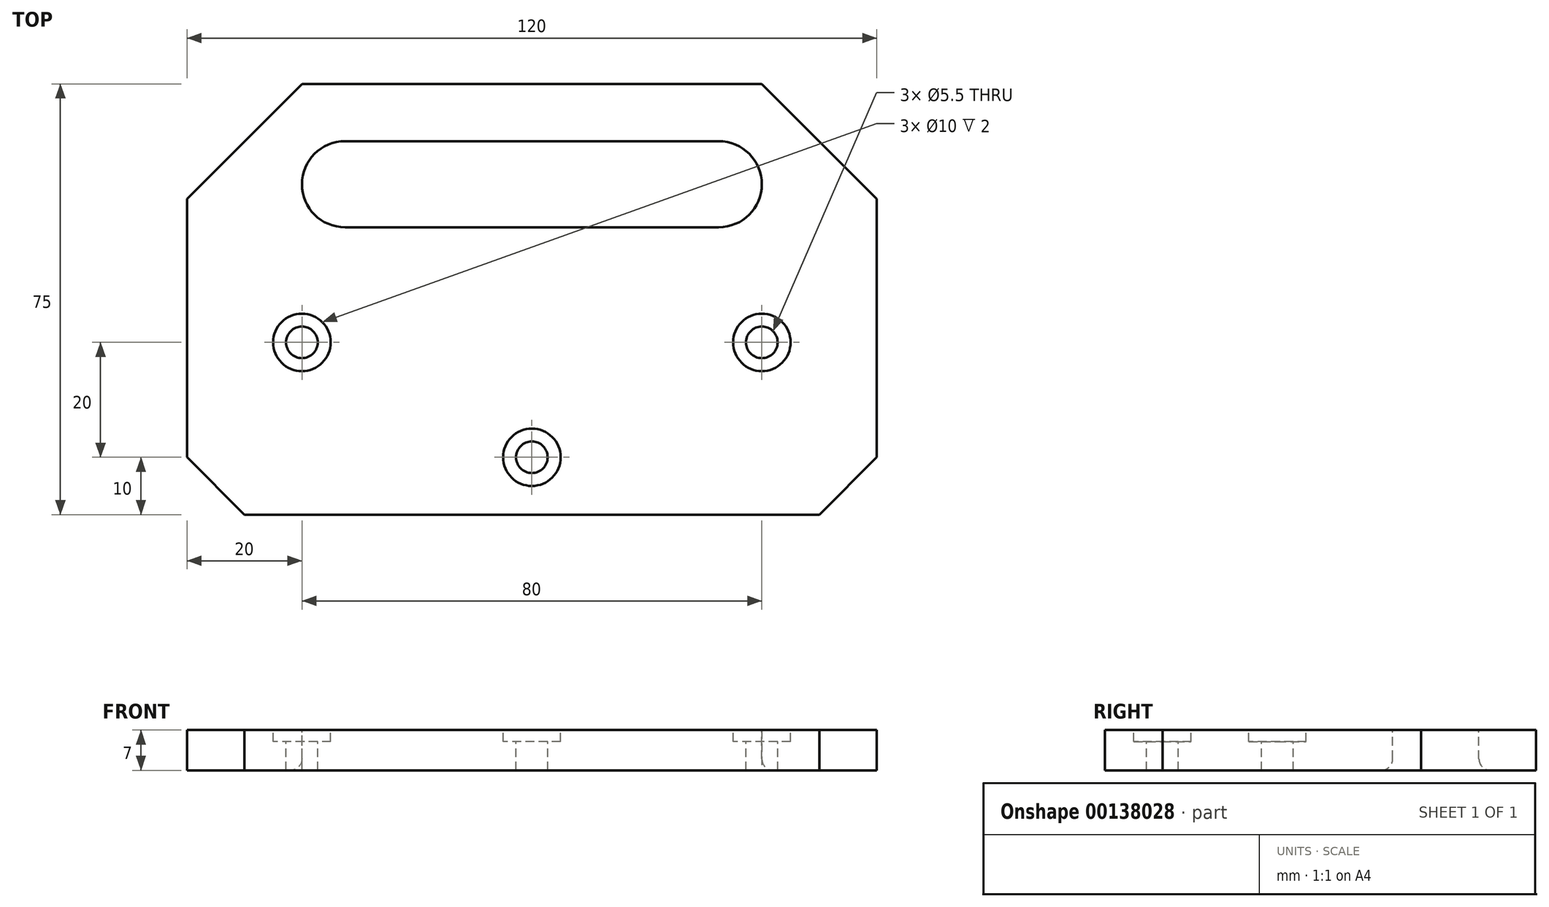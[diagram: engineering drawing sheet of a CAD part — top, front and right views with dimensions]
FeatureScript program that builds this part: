
annotation { "Feature Type Name" : "Feature", "Feature Type Description" : "" }
export const myFeature = defineFeature(function(context is Context, id is Id, definition is map)
    precondition{}
    {
        {
            var Q0;
            Q0=qCreatedBy(makeId("Top.planeOp"),FACE);
            var sketch = newSketch(context, id + "F0", { "sketchPlane" : qUnion([Q0])});
            skLineSegment(sketch, "E0.bottom", {"start": v(60, -37.5) * mm, "end": v(-60, -37.5) * mm});
            skLineSegment(sketch, "E0.top", {"start": v(60, 37.5) * mm, "end": v(-60, 37.5) * mm});
            skLineSegment(sketch, "E0.left", {"start": v(60, -37.5) * mm, "end": v(60, 37.5) * mm});
            skLineSegment(sketch, "E0.right", {"start": v(-60, -37.5) * mm, "end": v(-60, 37.5) * mm});
            skPoint(sketch, "E0.middle", {"position": v(0, 0) * mm});
            skSolve(sketch);
        }
        {
            var Q0;
            Q0=makeQuery(id+"F0.imprint","IMPRINT",FACE,{"disambiguationData":[TD([[makeQuery(id+"F0.imprint","IMPRINT",EDGE,{"derivedFrom":sQuery(id+"F0.wireOp",EDGE,"E0.bottom")}),-1.0]])]});
            extrude(context, id + "F1", {"entities" : qUnion([Q0]), "depth" : 7 * mm});
        }
        {
            var Q0;
            Q0=makeQuery(id+"F1.opExtrude","SWEPT_EDGE",EDGE,{"disambiguationData":[OSD([sQuery(id+"F0.wireOp",EDGE,"E0.top"),sQuery(id+"F0.wireOp",EDGE,"E0.right")])]});
            var Q1;
            Q1=makeQuery(id+"F1.opExtrude","SWEPT_EDGE",EDGE,{"disambiguationData":[OSD([sQuery(id+"F0.wireOp",EDGE,"E0.top"),sQuery(id+"F0.wireOp",EDGE,"E0.left")])]});
            chamfer(context, id + "F2", {"entities" : qUnion([Q0, Q1]), "width" : 20 * mm, "tangentPropagation" : true});
        }
        {
            var Q0;
            Q0=makeQuery(id+"F1.opExtrude","CAP_FACE",FACE,{"disambiguationData":[OSD([sQuery(id+"F0.wireOp",EDGE,"E0.bottom"),sQuery(id+"F0.wireOp",EDGE,"E0.top"),sQuery(id+"F0.wireOp",EDGE,"E0.left"),sQuery(id+"F0.wireOp",EDGE,"E0.right")])],"isStart":false});
            var sketch = newSketch(context, id + "F3", { "sketchPlane" : qUnion([Q0])});
            skLineSegment(sketch, "E1.bottom", {"start": v(32.5, 19.96) * mm, "end": v(-32.5, 19.96) * mm});
            skLineSegment(sketch, "E1.top", {"start": v(32.5, 20.04) * mm, "end": v(-32.5, 20.04) * mm});
            skLineSegment(sketch, "E1.left", {"start": v(32.5, 19.96) * mm, "end": v(32.5, 20.04) * mm});
            skLineSegment(sketch, "E1.right", {"start": v(-32.5, 19.96) * mm, "end": v(-32.5, 20.04) * mm});
            skPoint(sketch, "E1.middle", {"position": v(0, 20) * mm});
            skArc(sketch, "E2.0.startCap", {"start": v(32.5, 27.54) * mm, "mid": v(40, 20.04) * mm, "end": v(32.5, 12.54) * mm});
            skArc(sketch, "E2.0.endCap", {"start": v(-32.5, 12.54) * mm, "mid": v(-40, 20.04) * mm, "end": v(-32.5, 27.54) * mm});
            skLineSegment(sketch, "E2.0.left", {"start": v(32.5, 12.54) * mm, "end": v(-32.5, 12.54) * mm});
            skLineSegment(sketch, "E2.0.right", {"start": v(32.5, 27.54) * mm, "end": v(-32.5, 27.54) * mm});
            skSolve(sketch);
        }
        {
            var Q0;
            Q0=makeQuery(id+"F3.imprint","IMPRINT",FACE,{"disambiguationData":[TD([[makeQuery(id+"F3.imprint","IMPRINT",EDGE,{"derivedFrom":sQuery(id+"F3.wireOp",EDGE,"E1.bottom")}),1.0]])]});
            extrude(context, id + "F4", {"entities" : qUnion([Q0]), "operationType" : NewBodyOperationType.REMOVE, "oppositeDirection" : true, "depth" : 25 * mm});
        }
        {
            var Q0;
            Q0=makeQuery(id+"F4.boolean.opBoolean","COPY",FACE,{"derivedFrom":makeQuery(id+"F4.opExtrude","SWEPT_FACE",FACE,{"disambiguationData":[OSD([sQuery(id+"F3.wireOp",EDGE,"E1.top")])]})});
            extrude(context, id + "F5", {"entities" : qUnion([Q0]), "operationType" : NewBodyOperationType.REMOVE, "oppositeDirection" : true, "depth" : 5 * mm});
        }
        {
            var Q0;
            Q0=makeQuery(id+"F1.opExtrude","SWEPT_EDGE",EDGE,{"disambiguationData":[OSD([sQuery(id+"F0.wireOp",EDGE,"E0.bottom"),sQuery(id+"F0.wireOp",EDGE,"E0.right")])]});
            var Q1;
            Q1=makeQuery(id+"F1.opExtrude","SWEPT_EDGE",EDGE,{"disambiguationData":[OSD([sQuery(id+"F0.wireOp",EDGE,"E0.bottom"),sQuery(id+"F0.wireOp",EDGE,"E0.left")])]});
            chamfer(context, id + "F6", {"entities" : qUnion([Q0, Q1]), "width" : 10 * mm, "tangentPropagation" : true});
        }
        {
            var Q0;
            Q0=makeQuery(id+"F4.boolean.opBoolean","COPY",EDGE,{"derivedFrom":makeQuery(id+"F4.opExtrude","CAP_EDGE",EDGE,{"disambiguationData":[OSD([sQuery(id+"F3.wireOp",EDGE,"E2.0.startCap")])],"isStart":true})});
            var Q1;
            Q1=makeQuery(id+"F4.boolean.opBoolean","INTERSECT",EDGE,{"derivedFrom":[makeQuery(id+"F1.opExtrude","CAP_FACE",FACE,{"disambiguationData":[OSD([sQuery(id+"F0.wireOp",EDGE,"E0.bottom"),sQuery(id+"F0.wireOp",EDGE,"E0.top"),sQuery(id+"F0.wireOp",EDGE,"E0.left"),sQuery(id+"F0.wireOp",EDGE,"E0.right")])],"isStart":true}),makeQuery(id+"F4.opExtrude","SWEPT_FACE",FACE,{"disambiguationData":[OSD([sQuery(id+"F3.wireOp",EDGE,"E2.0.startCap")])]})]});
            fillet(context, id + "F7", {"entities" : qUnion([Q0, Q1]), "radius" : 2 * mm, "tangentPropagation" : true, "allowEdgeOverflow" : false});
        }
        {
            var Q0;
            {var subQ0=sQuery(id+"F0.wireOp",EDGE,"E0.right");var subQ1=sQuery(id+"F0.wireOp",EDGE,"E0.left");var subQ2=sQuery(id+"F0.wireOp",EDGE,"E0.top");var subQ3=sQuery(id+"F0.wireOp",EDGE,"E0.bottom");Q0=makeQuery(id+"F4.boolean.opBoolean","SPLIT",FACE,{"disambiguationData":[TD([makeQuery(id+"F1.opExtrude","SWEPT_FACE",FACE,{"disambiguationData":[OSD([subQ3])]})])],"derivedFrom":makeQuery(id+"F1.opExtrude","CAP_FACE",FACE,{"disambiguationData":[OSD([subQ3,subQ2,subQ1,subQ0])],"isStart":false})});}
            var sketch = newSketch(context, id + "F8", { "sketchPlane" : qUnion([Q0])});
            skPoint(sketch, "E3", {"position": v(0, -27.5) * mm});
            skPoint(sketch, "E4", {"position": v(-40, -7.5) * mm});
            skPoint(sketch, "E5", {"position": v(40, -7.5) * mm});
            skSolve(sketch);
        }
        {
            var Q0;
            Q0=sQuery(id+"F8.wireOp",VERTEX,"E4");
            var Q1;
            Q1=sQuery(id+"F8.wireOp",VERTEX,"E3");
            var Q2;
            Q2=sQuery(id+"F8.wireOp",VERTEX,"E5");
            var Q3;
            Q3=makeQuery(id+"F4.boolean.opBoolean","SPLIT",BODY,{"disambiguationData":[OD(0.0)],"derivedFrom":makeQuery(id+"F1.opExtrude","SWEPT_BODY",BODY,{"disambiguationData":[OSD([sQuery(id+"F0.wireOp",EDGE,"E0.bottom"),sQuery(id+"F0.wireOp",EDGE,"E0.top"),sQuery(id+"F0.wireOp",EDGE,"E0.left"),sQuery(id+"F0.wireOp",EDGE,"E0.right")])]})});
            hole(context, id + "F9", {"style" : HoleStyle.C_BORE, "endStyle" : HoleEndStyle.THROUGH, "holeDiameter" : 5.5 * mm, "cBoreDiameter" : 10 * mm, "cBoreDepth" : 2 * mm, "locations" : qUnion([Q0, Q1, Q2]), "scope" : qUnion([Q3]), "isTappedThrough" : true});
        }
    });
